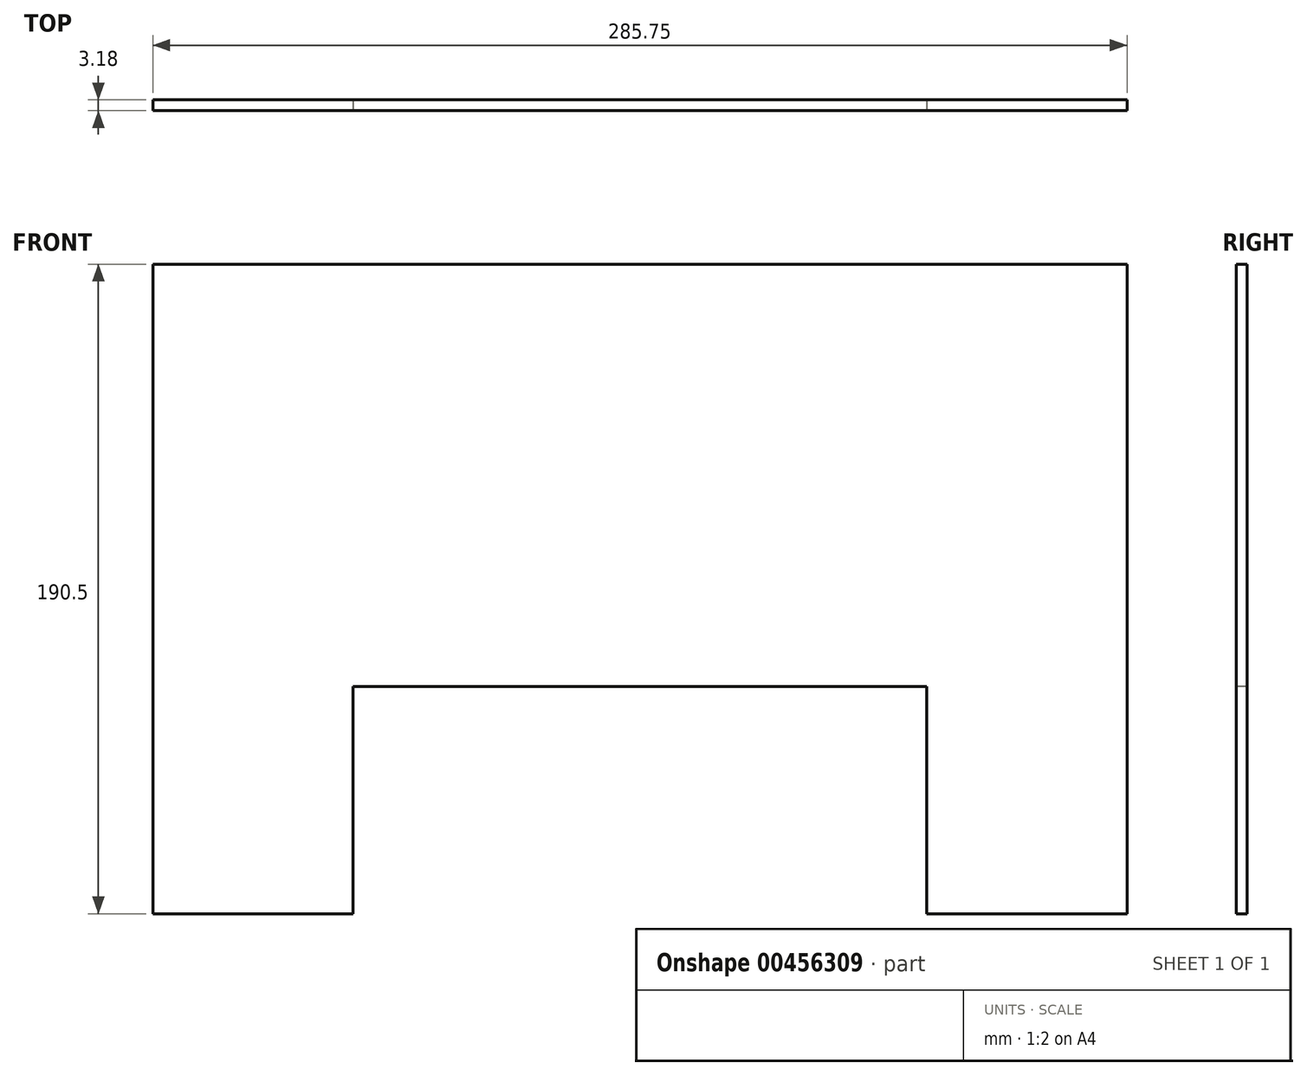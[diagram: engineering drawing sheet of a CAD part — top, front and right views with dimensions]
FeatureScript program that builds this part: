
annotation { "Feature Type Name" : "Feature", "Feature Type Description" : "" }
export const myFeature = defineFeature(function(context is Context, id is Id, definition is map)
    precondition{}
    {
        {
            var Q0;
            Q0=qCreatedBy(makeId("Top.planeOp"),FACE);
            var sketch = newSketch(context, id + "F0", { "sketchPlane" : qUnion([Q0])});
            skLineSegment(sketch, "E0.bottom", {"start": v(0, 0) * mm, "end": v(285.75, 0) * mm});
            skLineSegment(sketch, "E0.top", {"start": v(0, 3.18) * mm, "end": v(285.75, 3.18) * mm});
            skLineSegment(sketch, "E0.left", {"start": v(0, 0) * mm, "end": v(0, 3.18) * mm});
            skLineSegment(sketch, "E0.right", {"start": v(285.75, 0) * mm, "end": v(285.75, 3.18) * mm});
            skSolve(sketch);
        }
        {
            var Q0;
            Q0=makeQuery(id+"F0.imprint","IMPRINT",FACE,{"disambiguationData":[TD([[makeQuery(id+"F0.imprint","IMPRINT",EDGE,{"derivedFrom":sQuery(id+"F0.wireOp",EDGE,"E0.bottom")}),1.0]])]});
            extrude(context, id + "F1", {"entities" : qUnion([Q0]), "depth" : 190.5 * mm});
        }
        {
            var Q0;
            Q0=makeQuery(id+"F1.opExtrude","SWEPT_FACE",FACE,{"disambiguationData":[OSD([sQuery(id+"F0.wireOp",EDGE,"E0.bottom")])]});
            var sketch = newSketch(context, id + "F2", { "sketchPlane" : qUnion([Q0])});
            skLineSegment(sketch, "E1", {"start": v(0, 0) * mm, "end": v(58.74, 0) * mm});
            skLineSegment(sketch, "E2", {"start": v(285.75, 0) * mm, "end": v(227.01, 0) * mm});
            skLineSegment(sketch, "E3", {"start": v(58.74, 0) * mm, "end": v(58.74, 66.68) * mm});
            skLineSegment(sketch, "E4", {"start": v(58.74, 66.68) * mm, "end": v(227.01, 66.68) * mm});
            skLineSegment(sketch, "E5", {"start": v(227.01, 66.68) * mm, "end": v(227.01, 0) * mm});
            skSolve(sketch);
        }
        {
            var Q0;
            {var subQ0=sQuery(id+"F2.wireOp",EDGE,"E3");Q0=makeQuery(id+"F2.imprint","IMPRINT",FACE,{"disambiguationData":[TD([[makeQuery(id+"F2.imprint","IMPRINT",EDGE,{"derivedFrom":subQ0}),-1.0]])]});}
            extrude(context, id + "F3", {"entities" : qUnion([Q0]), "operationType" : NewBodyOperationType.REMOVE, "oppositeDirection" : true, "depth" : 25.4 * mm});
        }
    });
